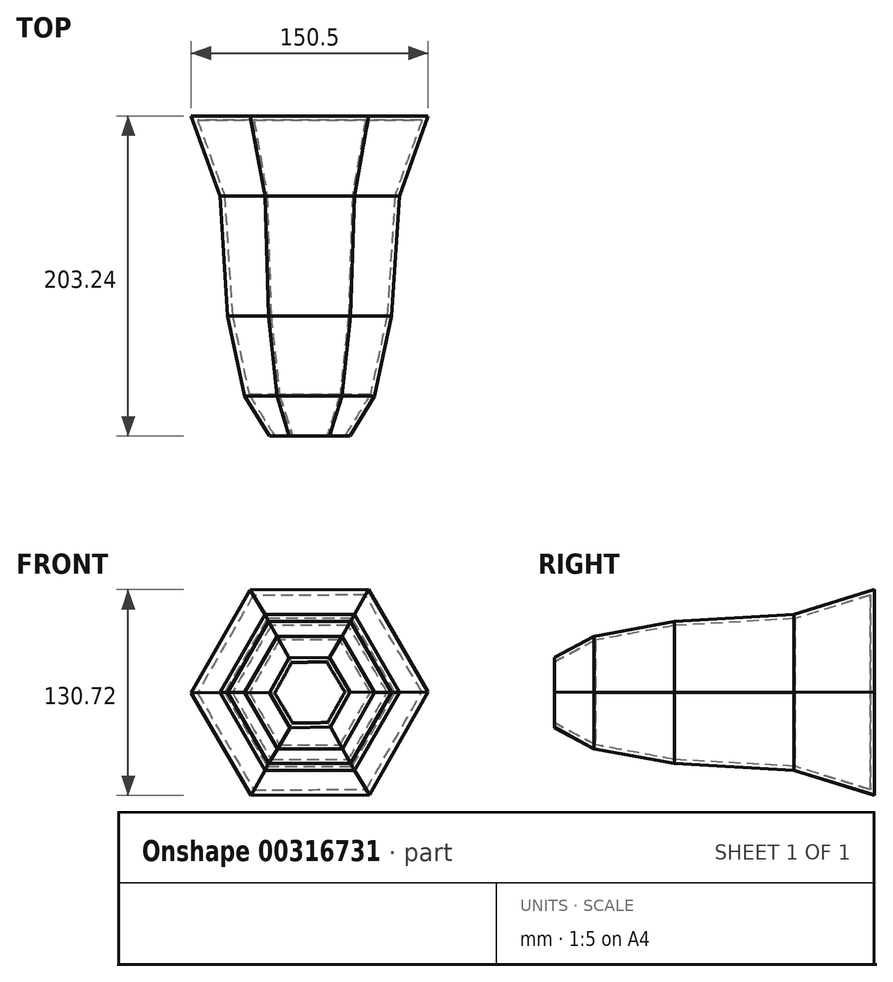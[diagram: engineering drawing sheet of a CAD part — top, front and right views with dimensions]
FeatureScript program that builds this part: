
annotation { "Feature Type Name" : "Feature", "Feature Type Description" : "" }
export const myFeature = defineFeature(function(context is Context, id is Id, definition is map)
    precondition{}
    {
        {
            var Q0;
            Q0=qCreatedBy(makeId("Front.planeOp"),FACE);
            var sketch = newSketch(context, id + "F0", { "sketchPlane" : qUnion([Q0])});
            skCircle(sketch, "E0.cCircle", {"center": v(0, 0) * mm, "radius": 65.17 * mm, "construction": true});
            skLineSegment(sketch, "E0.0", {"start": v(37.3, 65.36) * mm, "end": v(75.25, 0.37) * mm});
            skLineSegment(sketch, "E0.1", {"start": v(75.25, 0.37) * mm, "end": v(37.95, -64.98) * mm});
            skLineSegment(sketch, "E0.2", {"start": v(37.95, -64.98) * mm, "end": v(-37.3, -65.36) * mm});
            skLineSegment(sketch, "E0.3", {"start": v(-37.3, -65.36) * mm, "end": v(-75.25, -0.37) * mm});
            skLineSegment(sketch, "E0.4", {"start": v(-75.25, -0.37) * mm, "end": v(-37.95, 64.98) * mm});
            skLineSegment(sketch, "E0.5", {"start": v(-37.95, 64.98) * mm, "end": v(37.3, 65.36) * mm});
            skPoint(sketch, "E0.0.midPoint", {"position": v(56.28, 32.86) * mm});
            skSolve(sketch);
        }
        {
            var Q0;
            Q0=qCreatedBy(makeId("Front.planeOp"),FACE);
            cPlane(context, id + "F1", {"entities" : qUnion([Q0]), "cplaneType" : CPlaneType.OFFSET, "offset" : 50.8 * mm, "width" : 152.4 * mm, "height" : 152.4 * mm});
        }
        {
            var Q0;
            Q0=qCreatedBy(id+"F1.planeOp",FACE);
            var sketch = newSketch(context, id + "F2", { "sketchPlane" : qUnion([Q0])});
            skCircle(sketch, "E1.cCircle", {"center": v(0, 0) * mm, "radius": 49.42 * mm, "construction": true});
            skLineSegment(sketch, "E1.0", {"start": v(-28.53, 49.42) * mm, "end": v(28.53, 49.42) * mm});
            skLineSegment(sketch, "E1.1", {"start": v(28.53, 49.42) * mm, "end": v(57.06, 0) * mm});
            skLineSegment(sketch, "E1.2", {"start": v(57.06, 0) * mm, "end": v(28.53, -49.42) * mm});
            skLineSegment(sketch, "E1.3", {"start": v(28.53, -49.42) * mm, "end": v(-28.53, -49.42) * mm});
            skLineSegment(sketch, "E1.4", {"start": v(-28.53, -49.42) * mm, "end": v(-57.06, 0) * mm});
            skLineSegment(sketch, "E1.5", {"start": v(-57.06, 0) * mm, "end": v(-28.53, 49.42) * mm});
            skPoint(sketch, "E1.0.midPoint", {"position": v(0, 49.42) * mm});
            skSolve(sketch);
        }
        {
            var Q0;
            Q0=makeQuery(id+"F0.imprint","IMPRINT",FACE,{"disambiguationData":[TD([[makeQuery(id+"F0.imprint","IMPRINT",EDGE,{"derivedFrom":sQuery(id+"F0.wireOp",EDGE,"E0.0")}),-1.0]])]});
            var Q1;
            Q1=makeQuery(id+"F2.imprint","IMPRINT",FACE,{"disambiguationData":[TD([[makeQuery(id+"F2.imprint","IMPRINT",EDGE,{"derivedFrom":sQuery(id+"F2.wireOp",EDGE,"E1.0")}),-1.0]])]});
            loft(context, id + "F3", {"sheetProfilesArray" : [{ "sheetProfileEntities" : qUnion([Q0]) }, { "sheetProfileEntities" : qUnion([Q1]) }]});
        }
        {
            var Q0;
            Q0=qCreatedBy(id+"F1.planeOp",FACE);
            cPlane(context, id + "F4", {"entities" : qUnion([Q0]), "cplaneType" : CPlaneType.OFFSET, "offset" : 76.2 * mm, "width" : 152.4 * mm, "height" : 152.4 * mm});
        }
        {
            var Q0;
            Q0=qCreatedBy(id+"F4.planeOp",FACE);
            var sketch = newSketch(context, id + "F5", { "sketchPlane" : qUnion([Q0])});
            skCircle(sketch, "E2.cCircle", {"center": v(0, 0) * mm, "radius": 45.1 * mm, "construction": true});
            skLineSegment(sketch, "E2.0", {"start": v(26.04, 45.1) * mm, "end": v(52.08, 0) * mm});
            skLineSegment(sketch, "E2.1", {"start": v(52.08, 0) * mm, "end": v(26.04, -45.1) * mm});
            skLineSegment(sketch, "E2.2", {"start": v(26.04, -45.1) * mm, "end": v(-26.04, -45.1) * mm});
            skLineSegment(sketch, "E2.3", {"start": v(-26.04, -45.1) * mm, "end": v(-52.08, 0) * mm});
            skLineSegment(sketch, "E2.4", {"start": v(-52.08, 0) * mm, "end": v(-26.04, 45.1) * mm});
            skLineSegment(sketch, "E2.5", {"start": v(-26.04, 45.1) * mm, "end": v(26.04, 45.1) * mm});
            skPoint(sketch, "E2.0.midPoint", {"position": v(39.06, 22.55) * mm});
            skSolve(sketch);
        }
        {
            var Q1;
            Q1=makeQuery(id+"F3.opLoft","CAP_FACE",FACE,{"disambiguationData":[OSD([makeQuery(id+"F2.imprint","IMPRINT",FACE,{"disambiguationData":[TD([[makeQuery(id+"F2.imprint","IMPRINT",EDGE,{"derivedFrom":sQuery(id+"F2.wireOp",EDGE,"E1.0")}),-1.0]])]})])],"isStart":true});
            var Q2;
            Q2=makeQuery(id+"F5.imprint","IMPRINT",FACE,{"disambiguationData":[TD([[makeQuery(id+"F5.imprint","IMPRINT",EDGE,{"derivedFrom":sQuery(id+"F5.wireOp",EDGE,"E2.0")}),-1.0]])]});
            loft(context, id + "F6", {"operationType" : NewBodyOperationType.ADD, "sheetProfilesArray" : [{ "sheetProfileEntities" : qUnion([Q1]) }, { "sheetProfileEntities" : qUnion([Q2]) }]});
        }
        {
            var Q0;
            Q0=qCreatedBy(id+"F4.planeOp",FACE);
            cPlane(context, id + "F7", {"entities" : qUnion([Q0]), "cplaneType" : CPlaneType.OFFSET, "offset" : 50.8 * mm, "width" : 152.4 * mm, "height" : 152.4 * mm});
        }
        {
            var Q0;
            Q0=qCreatedBy(id+"F7.planeOp",FACE);
            var sketch = newSketch(context, id + "F8", { "sketchPlane" : qUnion([Q0])});
            skCircle(sketch, "E3.cCircle", {"center": v(0, 0) * mm, "radius": 35.72 * mm, "construction": true});
            skLineSegment(sketch, "E3.0", {"start": v(20.57, 35.75) * mm, "end": v(41.25, 0.06) * mm});
            skLineSegment(sketch, "E3.1", {"start": v(41.25, 0.06) * mm, "end": v(20.68, -35.7) * mm});
            skLineSegment(sketch, "E3.2", {"start": v(20.68, -35.7) * mm, "end": v(-20.57, -35.75) * mm});
            skLineSegment(sketch, "E3.3", {"start": v(-20.57, -35.75) * mm, "end": v(-41.25, -0.06) * mm});
            skLineSegment(sketch, "E3.4", {"start": v(-41.25, -0.06) * mm, "end": v(-20.68, 35.7) * mm});
            skLineSegment(sketch, "E3.5", {"start": v(-20.68, 35.7) * mm, "end": v(20.57, 35.75) * mm});
            skPoint(sketch, "E3.0.midPoint", {"position": v(30.9, 17.9) * mm});
            skSolve(sketch);
        }
        {
            var Q1;
            Q1=makeQuery(id+"F6.opLoft","CAP_FACE",FACE,{"disambiguationData":[OSD([makeQuery(id+"F5.imprint","IMPRINT",FACE,{"disambiguationData":[TD([[makeQuery(id+"F5.imprint","IMPRINT",EDGE,{"derivedFrom":sQuery(id+"F5.wireOp",EDGE,"E2.0")}),-1.0]])]})])],"isStart":true});
            var Q2;
            Q2=makeQuery(id+"F8.imprint","IMPRINT",FACE,{"disambiguationData":[TD([[makeQuery(id+"F8.imprint","IMPRINT",EDGE,{"derivedFrom":sQuery(id+"F8.wireOp",EDGE,"E3.0")}),-1.0]])]});
            loft(context, id + "F9", {"operationType" : NewBodyOperationType.ADD, "sheetProfilesArray" : [{ "sheetProfileEntities" : qUnion([Q1]) }, { "sheetProfileEntities" : qUnion([Q2]) }]});
        }
        {
            var Q0;
            Q0=qCreatedBy(id+"F7.planeOp",FACE);
            cPlane(context, id + "F10", {"entities" : qUnion([Q0]), "cplaneType" : CPlaneType.OFFSET, "offset" : 25.4 * mm, "width" : 152.4 * mm, "height" : 152.4 * mm});
        }
        {
            var Q0;
            Q0=qCreatedBy(id+"F10.planeOp",FACE);
            var sketch = newSketch(context, id + "F11", { "sketchPlane" : qUnion([Q0])});
            skCircle(sketch, "E4.cCircle", {"center": v(0, 0) * mm, "radius": 22.15 * mm, "construction": true});
            skLineSegment(sketch, "E4.0", {"start": v(12.46, 22.34) * mm, "end": v(25.58, 0.38) * mm});
            skLineSegment(sketch, "E4.1", {"start": v(25.58, 0.38) * mm, "end": v(13.12, -21.96) * mm});
            skLineSegment(sketch, "E4.2", {"start": v(13.12, -21.96) * mm, "end": v(-12.46, -22.34) * mm});
            skLineSegment(sketch, "E4.3", {"start": v(-12.46, -22.34) * mm, "end": v(-25.58, -0.38) * mm});
            skLineSegment(sketch, "E4.4", {"start": v(-25.58, -0.38) * mm, "end": v(-13.12, 21.96) * mm});
            skLineSegment(sketch, "E4.5", {"start": v(-13.12, 21.96) * mm, "end": v(12.46, 22.34) * mm});
            skPoint(sketch, "E4.0.midPoint", {"position": v(19.02, 11.36) * mm});
            skSolve(sketch);
        }
        {
            var Q1;
            Q1=makeQuery(id+"F9.opLoft","CAP_FACE",FACE,{"disambiguationData":[OSD([makeQuery(id+"F8.imprint","IMPRINT",FACE,{"disambiguationData":[TD([[makeQuery(id+"F8.imprint","IMPRINT",EDGE,{"derivedFrom":sQuery(id+"F8.wireOp",EDGE,"E3.0")}),-1.0]])]})])],"isStart":true});
            var Q2;
            Q2=makeQuery(id+"F11.imprint","IMPRINT",FACE,{"disambiguationData":[TD([[makeQuery(id+"F11.imprint","IMPRINT",EDGE,{"derivedFrom":sQuery(id+"F11.wireOp",EDGE,"E4.0")}),-1.0]])]});
            loft(context, id + "F12", {"operationType" : NewBodyOperationType.ADD, "sheetProfilesArray" : [{ "sheetProfileEntities" : qUnion([Q1]) }, { "sheetProfileEntities" : qUnion([Q2]) }]});
        }
        {
            var Q0;
            Q0=makeQuery(id+"F12.opLoft","CAP_FACE",FACE,{"disambiguationData":[OSD([makeQuery(id+"F11.imprint","IMPRINT",FACE,{"disambiguationData":[TD([[makeQuery(id+"F11.imprint","IMPRINT",EDGE,{"derivedFrom":sQuery(id+"F11.wireOp",EDGE,"E4.0")}),-1.0]])]})])],"isStart":true});
            shell(context, id + "F13", {"entities" : qUnion([Q0]), "thickness" : 2.54 * mm});
        }
    });
